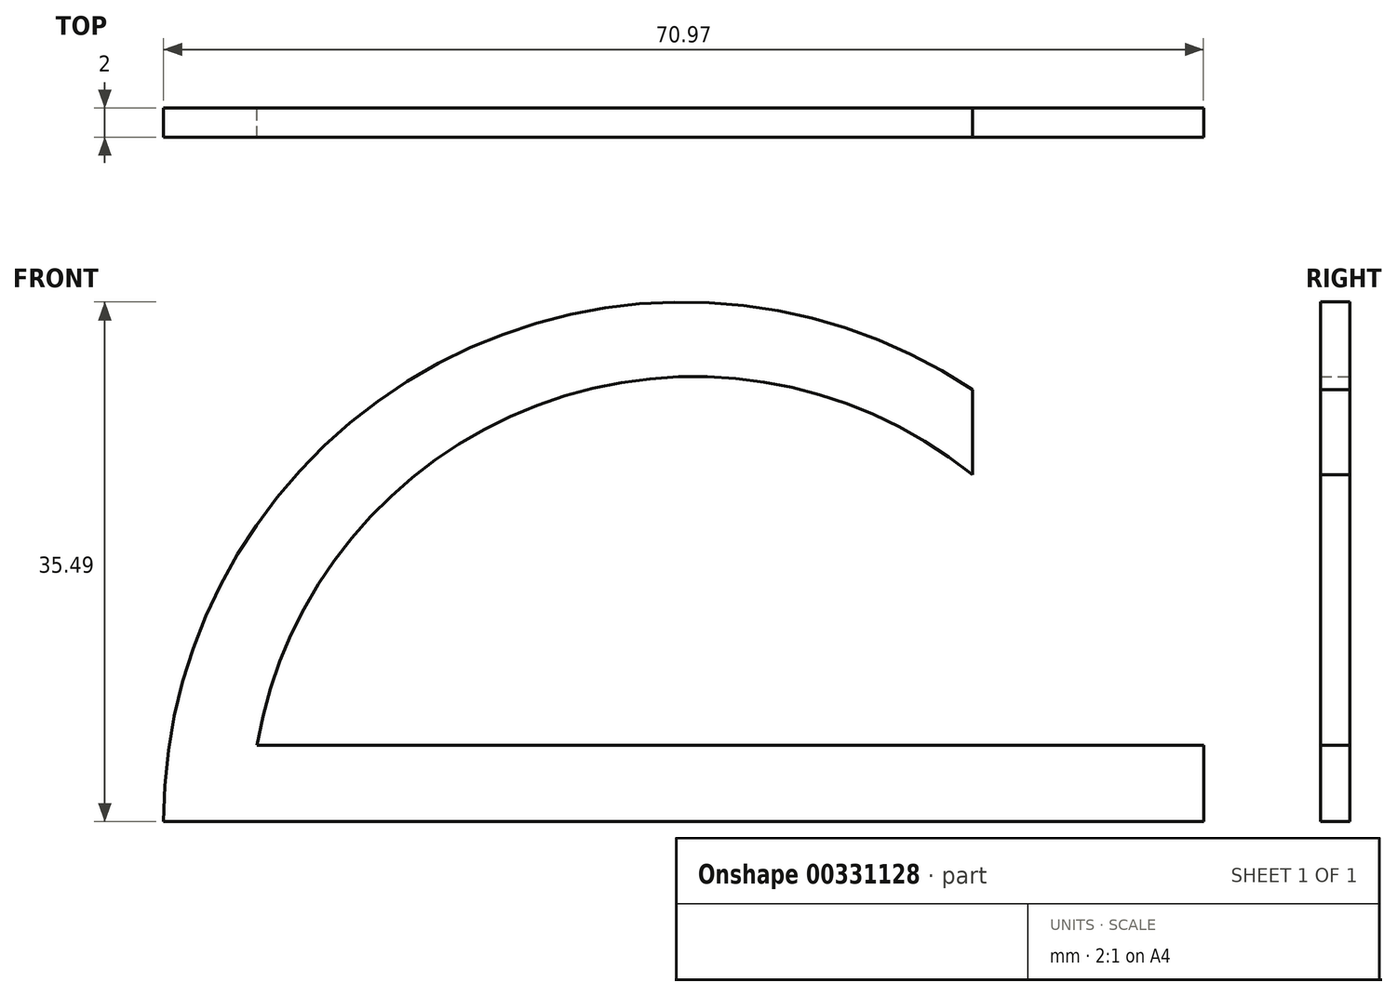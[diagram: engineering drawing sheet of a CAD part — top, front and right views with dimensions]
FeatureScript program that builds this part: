
annotation { "Feature Type Name" : "Feature", "Feature Type Description" : "" }
export const myFeature = defineFeature(function(context is Context, id is Id, definition is map)
    precondition{}
    {
        {
            var Q0;
            Q0=qCreatedBy(makeId("Front.planeOp"),FACE);
            var sketch = newSketch(context, id + "F0", { "sketchPlane" : qUnion([Q0])});
            skLineSegment(sketch, "E0", {"start": v(0, 0) * mm, "end": v(70.97, 0) * mm});
            skArc(sketch, "E1", {"start": v(55.2, 29.5) * mm, "mid": v(18.76, 31.3) * mm, "end": v(0, 0) * mm});
            skLineSegment(sketch, "E2", {"start": v(70.97, 0) * mm, "end": v(70.97, 0) * mm});
            skLineSegment(sketch, "E3", {"start": v(70.97, 0) * mm, "end": v(70.97, 5.21) * mm});
            skLineSegment(sketch, "E4", {"start": v(70.97, 5.21) * mm, "end": v(6.37, 5.21) * mm});
            skArc(sketch, "E5", {"start": v(55.2, 23.69) * mm, "mid": v(25.5, 28.43) * mm, "end": v(6.37, 5.21) * mm});
            skLineSegment(sketch, "E6", {"start": v(55.2, 29.5) * mm, "end": v(55.2, 23.69) * mm});
            skArc(sketch, "E7.trimOffspring", {"start": v(5.94, 0) * mm, "mid": v(5.95, -0.19) * mm, "end": v(5.95, -0.37) * mm});
            skSolve(sketch);
        }
        {
            var Q0;
            {var subQ1=sQuery(id+"F0.wireOp",EDGE,"E1");Q0=makeQuery(id+"F0.imprint","IMPRINT",FACE,{"disambiguationData":[TD([[makeQuery(id+"F0.imprint","IMPRINT",EDGE,{"derivedFrom":subQ1}),1.0]])]});}
            extrude(context, id + "F1", {"entities" : qUnion([Q0]), "depth" : 2 * mm});
        }
    });
